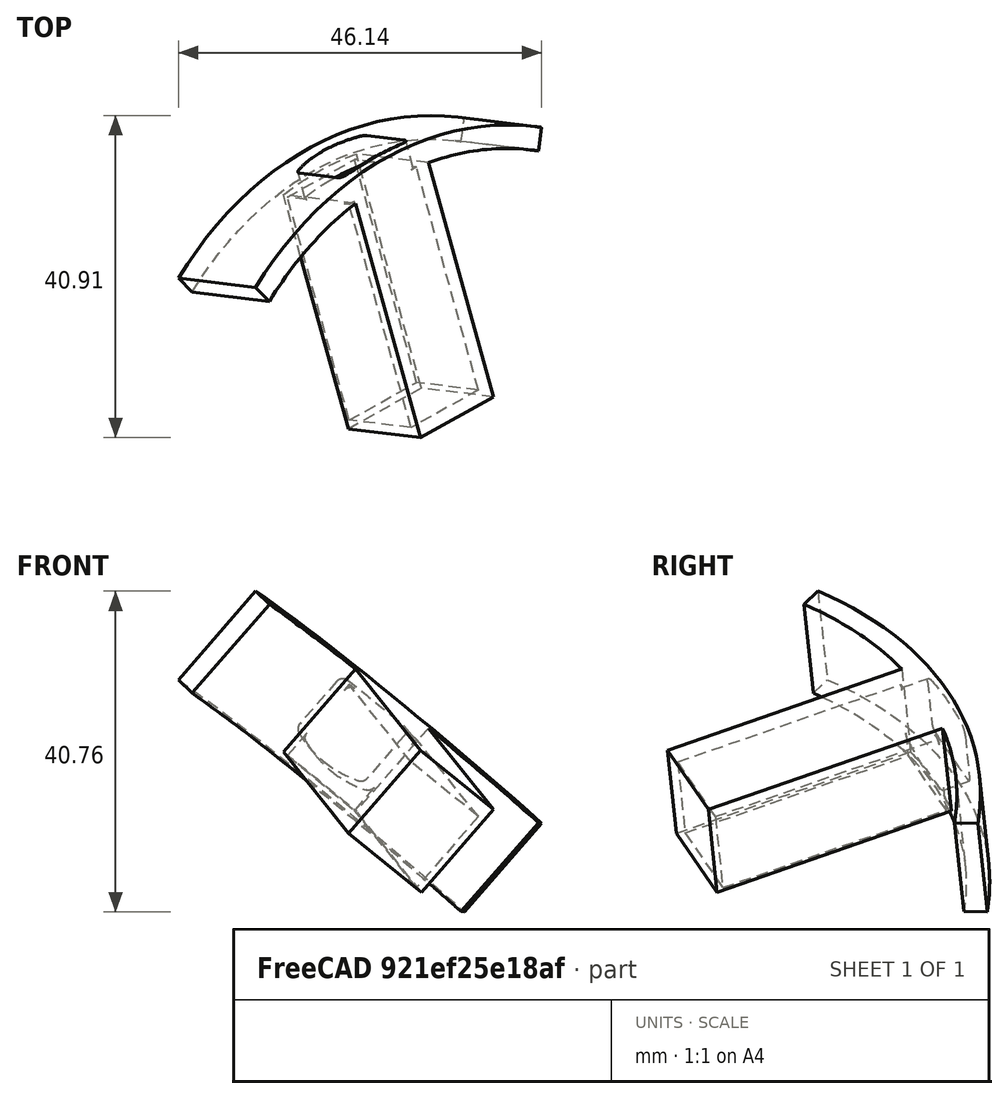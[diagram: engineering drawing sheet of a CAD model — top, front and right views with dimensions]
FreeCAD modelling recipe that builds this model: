
FCSTD DOCUMENT  (FreeCAD 0.16R4924 (Git))
Label: interior_servo_bay_v3p2
License: All rights reserved
LicenseURL: http://en.wikipedia.org/wiki/All_rights_reserved
objects: Part::Cut×3, Part::Cylinder×2, Part::Feature×2, Part::Extrusion×2, Part::MultiFuse×2, Part::Box×2, Part::Thickness×1
note: 14 computed .brp shape members not serialized (recipe doc carries the construction recipe); baked Part::Feature solids carry a one-line shape summary decoded from their .brp

FEATURE [Part::Cylinder] Cylinder  label="bottle_wall"
  Angle = 60
  Height = 15
  Placement = pos=(8.5,-7,0) rot=(0,0,1;1.0472rad)
  Radius = 51
FEATURE [Part::Cylinder] Cylinder001  label="bottle_wall001"
  Angle = 60
  Height = 15
  Placement = pos=(8.5,-7,0) rot=(0,0,1;1.0472rad)
  Radius = 48
FEATURE [Part::Cut] Cut  label="bottle_wall_composite"
  Base = -> Cylinder
  Placement = pos=(0,-2,0) rot=(0,0,1;0rad)
  Tool = -> Cylinder001
FEATURE [Part::Feature] Common_cs  label="pin_cs"
  Placement = pos=(3.5,35,2) rot=(0,0,1;0rad)
  shape: bbox 10 x 2e-07 x 8 mm, 0 faces, 0 solids (baked)
FEATURE [Part::Extrusion] Extrude
  Base = -> Common_cs
  Dir = (0,5,0)
  Solid = true
FEATURE [Part::Thickness] Thickness
  Faces = -> Extrude [Face7]
  Intersection = false
  Join = 0
  Mode = 0
  SelfIntersection = false
  Value = 1
FEATURE [Part::Feature] Common_cs001  label="pin_cs001"
  Placement = pos=(3.5,35,2) rot=(0,0,1;0rad)
  shape: bbox 10 x 2e-07 x 8 mm, 0 faces, 0 solids (baked)
FEATURE [Part::Extrusion] Extrude001
  Base = -> Common_cs001
  Dir = (0,5,0)
  Solid = true
FEATURE [Part::MultiFuse] Fusion  label="bolt_bottle_side_opening"
  Placement = pos=(0,-7,1) rot=(0,0,1;0rad)
  Shapes = -> [Thickness,Extrude,Extrude001]
FEATURE [Part::Box] Box  label="pullBay"
  Height = 15
  Length = 12
  Placement = pos=(2.5,7,2) rot=(0,0,1;0rad)
  Width = 31
FEATURE [Part::Box] Box001  label="Case"
  Height = 14
  Length = 13
  Placement = pos=(2,6,0) rot=(0,0,1;0rad)
  Width = 34
FEATURE [Part::Cut] Cut001  label="cut bay from case"
  Base = -> Box001
  Tool = -> Box
FEATURE [Part::MultiFuse] Fusion001  label="wall plus case"
  Shapes = -> [Cut,Cut001]
FEATURE [Part::Cut] Cut002  label="hole cut out of case"
  Base = -> Fusion001
  Placement = pos=(0,0,0) rot=(-0.188305,0.975433,0.114334;3.82553rad)
  Tool = -> Fusion
